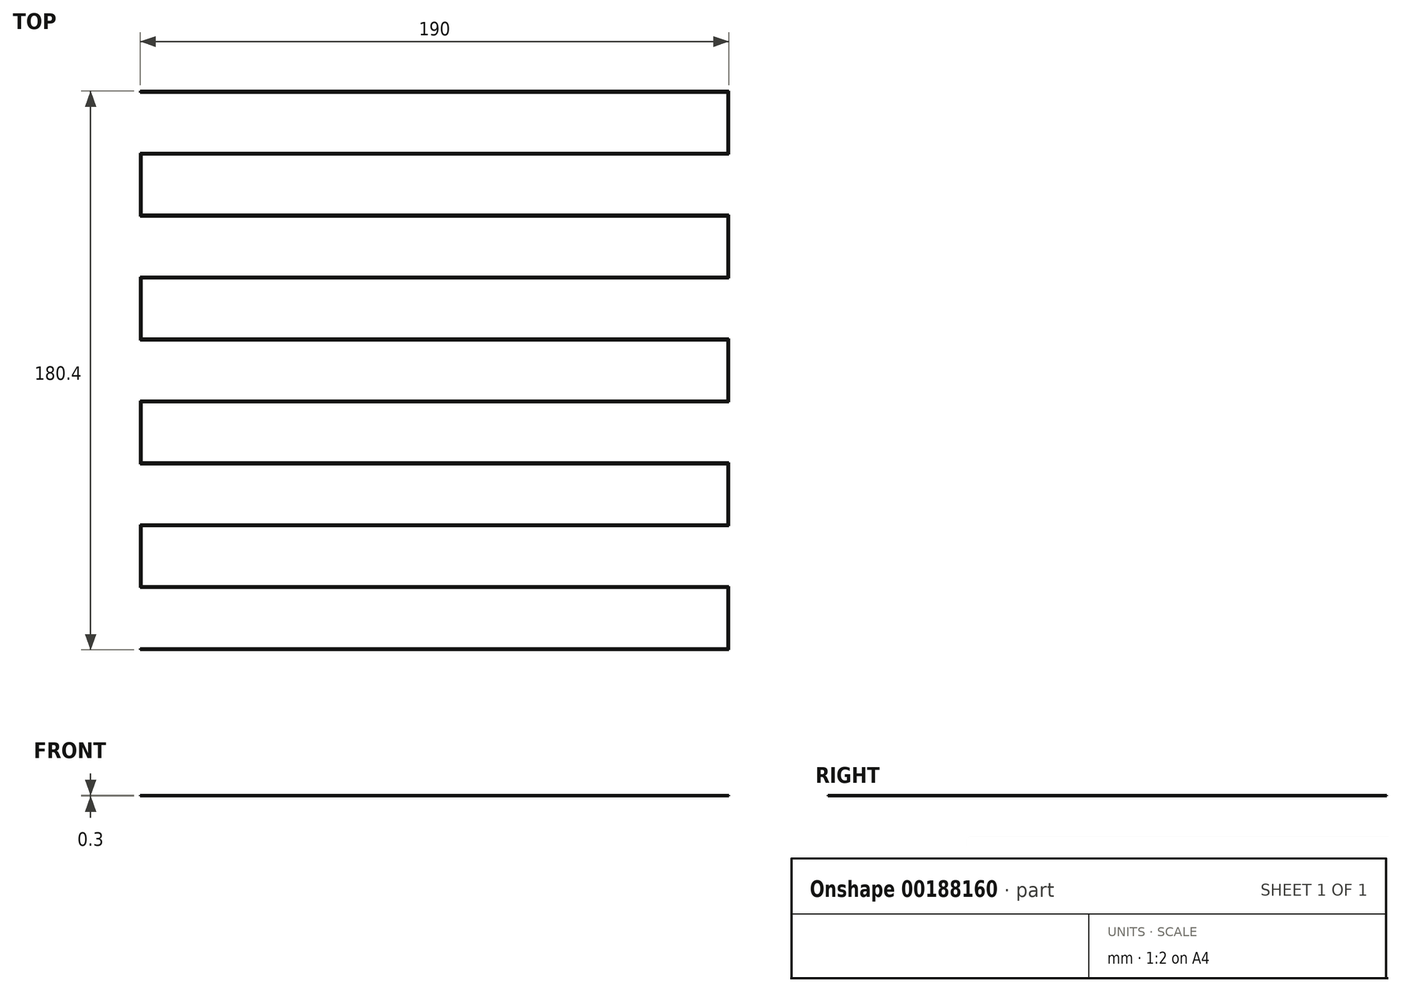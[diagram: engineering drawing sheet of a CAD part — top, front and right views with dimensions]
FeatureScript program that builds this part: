
annotation { "Feature Type Name" : "Feature", "Feature Type Description" : "" }
export const myFeature = defineFeature(function(context is Context, id is Id, definition is map)
    precondition{}
    {
        {
            var Q0;
            Q0=qCreatedBy(makeId("Top.planeOp"),FACE);
            var sketch = newSketch(context, id + "F0", { "sketchPlane" : qUnion([Q0])});
            skLineSegment(sketch, "E0.bottom", {"start": v(-90, 48.86) * mm, "end": v(100, 48.86) * mm});
            skLineSegment(sketch, "E0.top", {"start": v(-90, 48.46) * mm, "end": v(99.6, 48.46) * mm});
            skLineSegment(sketch, "E0.left", {"start": v(-90, 48.86) * mm, "end": v(-90, 48.46) * mm});
            skLineSegment(sketch, "E0.right", {"start": v(100, 48.86) * mm, "end": v(100, 48.46) * mm});
            skLineSegment(sketch, "E1", {"start": v(100, 48.46) * mm, "end": v(100, 28.46) * mm});
            skLineSegment(sketch, "E2", {"start": v(100, 28.46) * mm, "end": v(-89.6, 28.46) * mm});
            skLineSegment(sketch, "E3", {"start": v(-90, 28.46) * mm, "end": v(-90, 28.86) * mm});
            skLineSegment(sketch, "E4", {"start": v(-90, 28.86) * mm, "end": v(99.6, 28.86) * mm});
            skLineSegment(sketch, "E5", {"start": v(99.6, 28.86) * mm, "end": v(99.6, 48.46) * mm});
            skLineSegment(sketch, "E6", {"start": v(-90, 28.46) * mm, "end": v(-90, 8.86) * mm});
            skLineSegment(sketch, "E7", {"start": v(-89.6, 8.86) * mm, "end": v(-89.6, 28.46) * mm});
            skLineSegment(sketch, "E8.0.1.0", {"start": v(-90, -11.54) * mm, "end": v(-90, -11.14) * mm});
            skLineSegment(sketch, "E8.0.1.1", {"start": v(-90, -11.54) * mm, "end": v(-90, -31.14) * mm});
            skLineSegment(sketch, "E8.0.1.2", {"start": v(-89.6, -31.14) * mm, "end": v(-89.6, -11.54) * mm});
            skLineSegment(sketch, "E8.0.1.3", {"start": v(100, -11.54) * mm, "end": v(-89.6, -11.54) * mm});
            skLineSegment(sketch, "E8.0.1.4", {"start": v(-90, -11.14) * mm, "end": v(99.6, -11.14) * mm});
            skLineSegment(sketch, "E8.0.1.6", {"start": v(-90, 8.86) * mm, "end": v(-90, 8.46) * mm});
            skLineSegment(sketch, "E8.0.1.7", {"start": v(-89.6, 8.86) * mm, "end": v(100, 8.86) * mm});
            skLineSegment(sketch, "E8.0.1.8", {"start": v(-90, 8.46) * mm, "end": v(99.6, 8.46) * mm});
            skLineSegment(sketch, "E8.0.1.9", {"start": v(100, 8.46) * mm, "end": v(100, -11.54) * mm});
            skLineSegment(sketch, "E8.0.1.10", {"start": v(99.6, -11.14) * mm, "end": v(99.6, 8.46) * mm});
            skLineSegment(sketch, "E8.0.1.11", {"start": v(100, 8.86) * mm, "end": v(100, 8.46) * mm});
            skLineSegment(sketch, "E8.0.2.0", {"start": v(-90, -51.54) * mm, "end": v(-90, -51.14) * mm});
            skLineSegment(sketch, "E8.0.2.1", {"start": v(-90, -51.54) * mm, "end": v(-90, -71.14) * mm});
            skLineSegment(sketch, "E8.0.2.2", {"start": v(-89.6, -71.14) * mm, "end": v(-89.6, -51.54) * mm});
            skLineSegment(sketch, "E8.0.2.3", {"start": v(100, -51.54) * mm, "end": v(-89.6, -51.54) * mm});
            skLineSegment(sketch, "E8.0.2.4", {"start": v(-90, -51.14) * mm, "end": v(99.6, -51.14) * mm});
            skLineSegment(sketch, "E8.0.2.6", {"start": v(-90, -31.14) * mm, "end": v(-90, -31.54) * mm});
            skLineSegment(sketch, "E8.0.2.7", {"start": v(-89.6, -31.14) * mm, "end": v(100, -31.14) * mm});
            skLineSegment(sketch, "E8.0.2.8", {"start": v(-90, -31.54) * mm, "end": v(99.6, -31.54) * mm});
            skLineSegment(sketch, "E8.0.2.9", {"start": v(100, -31.54) * mm, "end": v(100, -51.54) * mm});
            skLineSegment(sketch, "E8.0.2.10", {"start": v(99.6, -51.14) * mm, "end": v(99.6, -31.54) * mm});
            skLineSegment(sketch, "E8.0.2.11", {"start": v(100, -31.14) * mm, "end": v(100, -31.54) * mm});
            skLineSegment(sketch, "E8.0.3.0", {"start": v(-90, -91.54) * mm, "end": v(-90, -91.14) * mm});
            skLineSegment(sketch, "E8.0.3.1", {"start": v(-90, -91.54) * mm, "end": v(-90, -111.14) * mm});
            skLineSegment(sketch, "E8.0.3.2", {"start": v(-89.6, -111.14) * mm, "end": v(-89.6, -91.54) * mm});
            skLineSegment(sketch, "E8.0.3.3", {"start": v(100, -91.54) * mm, "end": v(-89.6, -91.54) * mm});
            skLineSegment(sketch, "E8.0.3.4", {"start": v(-90, -91.14) * mm, "end": v(99.6, -91.14) * mm});
            skLineSegment(sketch, "E8.0.3.5", {"start": v(-89.6, -111.14) * mm, "end": v(-90, -111.14) * mm});
            skLineSegment(sketch, "E8.0.3.6", {"start": v(-90, -71.14) * mm, "end": v(-90, -71.54) * mm});
            skLineSegment(sketch, "E8.0.3.7", {"start": v(-89.6, -71.14) * mm, "end": v(100, -71.14) * mm});
            skLineSegment(sketch, "E8.0.3.8", {"start": v(-90, -71.54) * mm, "end": v(99.6, -71.54) * mm});
            skLineSegment(sketch, "E8.0.3.9", {"start": v(100, -71.54) * mm, "end": v(100, -91.54) * mm});
            skLineSegment(sketch, "E8.0.3.10", {"start": v(99.6, -91.14) * mm, "end": v(99.6, -71.54) * mm});
            skLineSegment(sketch, "E8.0.3.11", {"start": v(100, -71.14) * mm, "end": v(100, -71.54) * mm});
            skLineSegment(sketch, "E8.0.4.0", {"start": v(-90, -131.54) * mm, "end": v(-90, -131.14) * mm});
            skLineSegment(sketch, "E8.0.4.3", {"start": v(100, -131.54) * mm, "end": v(-89.6, -131.54) * mm});
            skLineSegment(sketch, "E8.0.4.4", {"start": v(-90, -131.14) * mm, "end": v(99.6, -131.14) * mm});
            skLineSegment(sketch, "E8.0.4.6", {"start": v(-90, -111.14) * mm, "end": v(-90, -111.54) * mm});
            skLineSegment(sketch, "E8.0.4.7", {"start": v(-90, -111.14) * mm, "end": v(100, -111.14) * mm});
            skLineSegment(sketch, "E8.0.4.8", {"start": v(-90, -111.54) * mm, "end": v(99.6, -111.54) * mm});
            skLineSegment(sketch, "E8.0.4.9", {"start": v(100, -111.54) * mm, "end": v(100, -131.54) * mm});
            skLineSegment(sketch, "E8.0.4.10", {"start": v(99.6, -131.14) * mm, "end": v(99.6, -111.54) * mm});
            skLineSegment(sketch, "E8.0.4.11", {"start": v(100, -111.14) * mm, "end": v(100, -111.54) * mm});
            skLineSegment(sketch, "E8.direction1", {"start": v(-89.6, 8.86) * mm, "end": v(-75, 8.86) * mm, "construction": true});
            skLineSegment(sketch, "E8.direction2", {"start": v(-90, 8.86) * mm, "end": v(-90, -31.14) * mm, "construction": true});
            skLineSegment(sketch, "E9", {"start": v(-99.6, -331.54) * mm, "end": v(-100, -331.54) * mm});
            skLineSegment(sketch, "E10", {"start": v(-89.6, -131.54) * mm, "end": v(-90, -131.54) * mm});
            skSolve(sketch);
        }
        {
            var Q0;
            Q0 = qSketchRegion(id + "F0", true);
            extrude(context, id + "F1", {"entities" : qUnion([Q0]), "depth" : 0.3 * mm});
        }
    });
